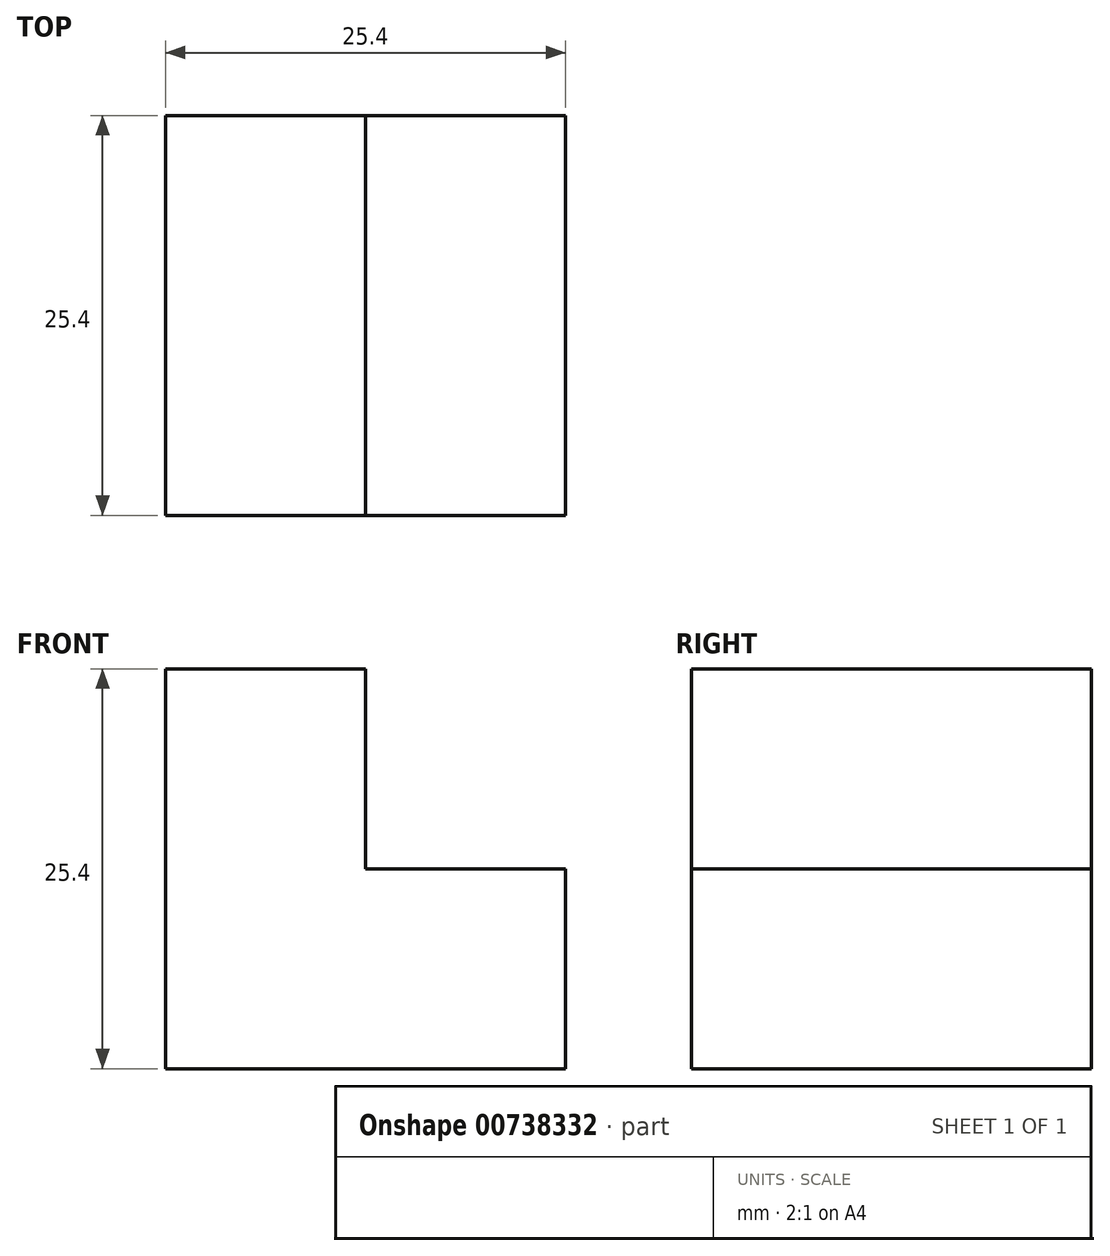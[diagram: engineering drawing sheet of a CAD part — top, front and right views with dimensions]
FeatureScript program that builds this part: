
annotation { "Feature Type Name" : "Feature", "Feature Type Description" : "" }
export const myFeature = defineFeature(function(context is Context, id is Id, definition is map)
    precondition{}
    {
        {
            var Q0;
            Q0=qCreatedBy(makeId("Front.planeOp"),FACE);
            var sketch = newSketch(context, id + "F0", { "sketchPlane" : qUnion([Q0])});
            skLineSegment(sketch, "E0", {"start": v(0, 16.4) * mm, "end": v(0, 0) * mm});
            skLineSegment(sketch, "E1", {"start": v(0, 0) * mm, "end": v(25.4, 0) * mm});
            skLineSegment(sketch, "E2", {"start": v(25.4, 0) * mm, "end": v(25.4, 12.7) * mm});
            skLineSegment(sketch, "E3", {"start": v(25.4, 12.7) * mm, "end": v(12.7, 12.7) * mm});
            skLineSegment(sketch, "E4", {"start": v(12.7, 12.7) * mm, "end": v(12.7, 25.4) * mm});
            skLineSegment(sketch, "E5", {"start": v(12.7, 25.4) * mm, "end": v(0, 25.4) * mm});
            skLineSegment(sketch, "E6", {"start": v(0, 25.4) * mm, "end": v(0, 16.4) * mm});
            skSolve(sketch);
        }
        {
            var Q0;
            Q0 = qSketchRegion(id + "F0", true);
            extrude(context, id + "F1", {"entities" : qUnion([Q0]), "depth" : 25.4 * mm, "offsetDistance" : 25.4 * mm});
        }
    });
